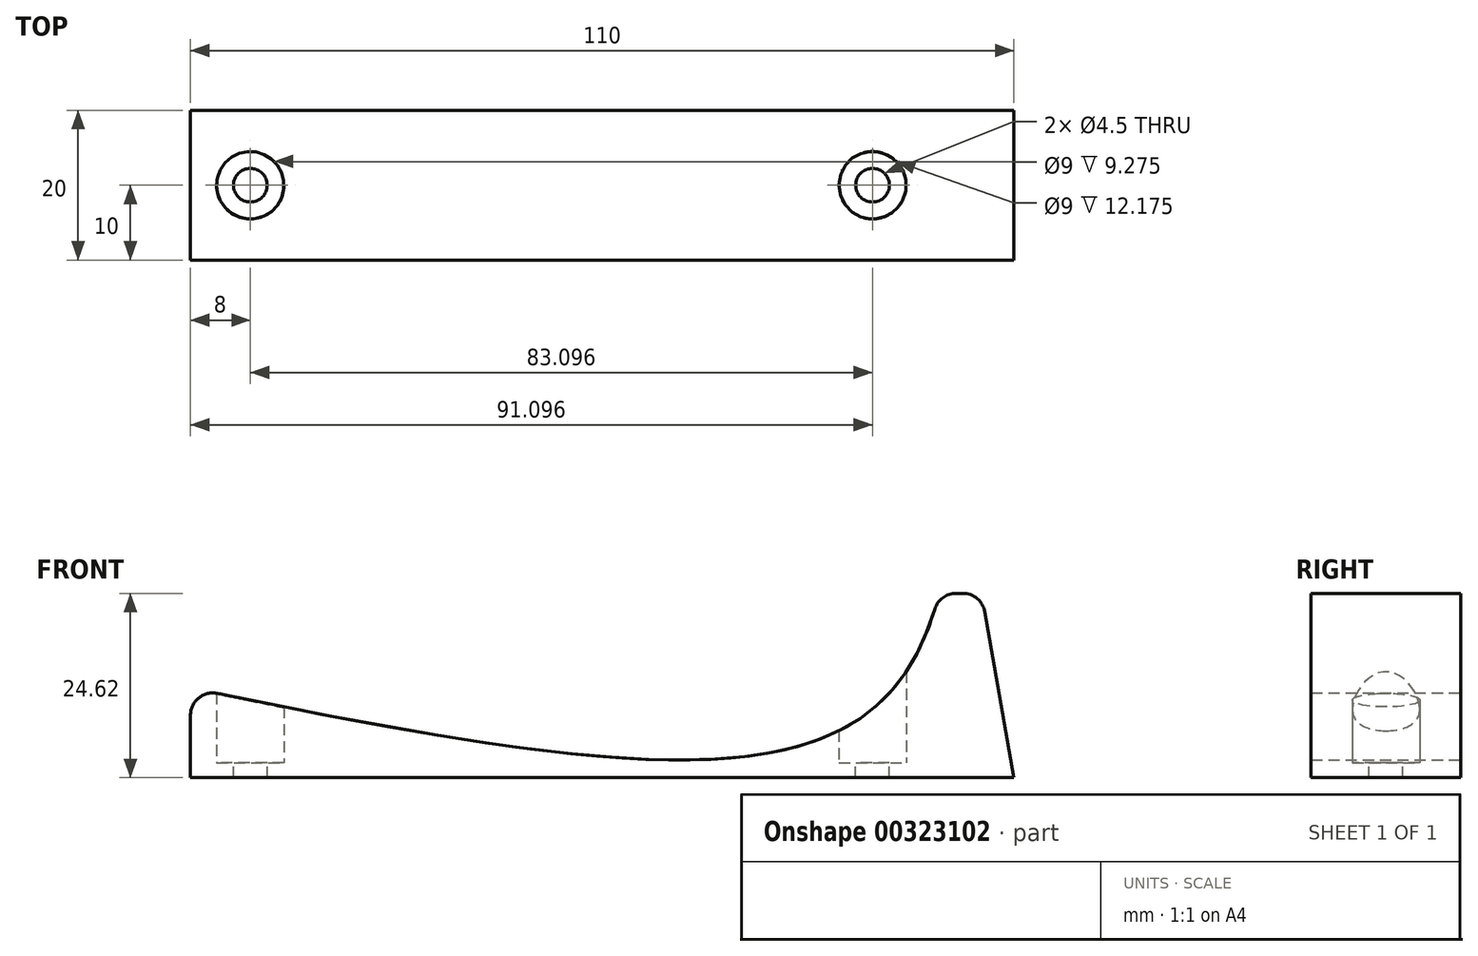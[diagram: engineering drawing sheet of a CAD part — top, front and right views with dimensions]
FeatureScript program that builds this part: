
annotation { "Feature Type Name" : "Feature", "Feature Type Description" : "" }
export const myFeature = defineFeature(function(context is Context, id is Id, definition is map)
    precondition{}
    {
        {
            var Q0;
            Q0=qCreatedBy(makeId("Front.planeOp"),FACE);
            var sketch = newSketch(context, id + "F0", { "sketchPlane" : qUnion([Q0])});
            skFitSpline(sketch, "E0", {"points": [v(0, 12) * mm, v(101.32, 64.38) * mm], "startDerivative": vector(270.11, -56.3) * mm, "endDerivative": vector(-14.41, 200.62) * mm});
            skLineSegment(sketch, "E1", {"start": v(105.66, 24.62) * mm, "end": v(110, 0) * mm});
            skLineSegment(sketch, "E2", {"start": v(110, 0) * mm, "end": v(0, 0) * mm});
            skLineSegment(sketch, "E3", {"start": v(0, 0) * mm, "end": v(0, 12) * mm});
            skLineSegment(sketch, "E4", {"start": v(100, 24.62) * mm, "end": v(105.66, 24.62) * mm});
            skPoint(sketch, "E4.endSnap0", {"position": v(105.66, 32.19) * mm});
            skSolve(sketch);
        }
        {
            var Q0;
            Q0=makeQuery(id+"F0.imprint","IMPRINT",FACE,{"disambiguationData":[TD([[makeQuery(id+"F0.imprint","IMPRINT",EDGE,{"derivedFrom":sQuery(id+"F0.wireOp",EDGE,"E0")}),-1.0]])]});
            extrude(context, id + "F1", {"entities" : qUnion([Q0]), "endBound" : BoundingType.SYMMETRIC, "depth" : 20 * mm});
        }
        {
            var Q0;
            Q0=makeQuery(id+"F1.opExtrude","SWEPT_EDGE",EDGE,{"disambiguationData":[OSD([sQuery(id+"F0.wireOp",EDGE,"E0"),sQuery(id+"F0.wireOp",EDGE,"E3")])]});
            var Q1;
            Q1=makeQuery(id+"F1.opExtrude","SWEPT_EDGE",EDGE,{"disambiguationData":[OSD([sQuery(id+"F0.wireOp",EDGE,"E0"),sQuery(id+"F0.wireOp",EDGE,"E4")])]});
            var Q2;
            Q2=makeQuery(id+"F1.opExtrude","SWEPT_EDGE",EDGE,{"disambiguationData":[OSD([sQuery(id+"F0.wireOp",EDGE,"E1"),sQuery(id+"F0.wireOp",EDGE,"E4")])]});
            fillet(context, id + "F2", {"entities" : qUnion([Q0, Q1, Q2]), "radius" : 3 * mm, "tangentPropagation" : true, "allowEdgeOverflow" : false});
        }
        {
            var Q0;
            Q0=qCreatedBy(makeId("Top.planeOp"),FACE);
            cPlane(context, id + "F3", {"entities" : qUnion([Q0]), "cplaneType" : CPlaneType.OFFSET, "offset" : 2 * mm, "width" : 150 * mm, "height" : 150 * mm});
        }
        {
            var Q0;
            Q0=qCreatedBy(id+"F3.planeOp",FACE);
            var sketch = newSketch(context, id + "F4", { "sketchPlane" : qUnion([Q0])});
            skCircle(sketch, "E5", {"center": v(8, 0) * mm, "radius": 4.5 * mm});
            skCircle(sketch, "E6", {"center": v(91.1, 0) * mm, "radius": 4.5 * mm});
            skSolve(sketch);
        }
        {
            var Q0;
            Q0 = qSketchRegion(id + "F4", true);
            extrude(context, id + "F5", {"entities" : qUnion([Q0]), "operationType" : NewBodyOperationType.REMOVE, "endBound" : BoundingType.THROUGH_ALL, "depth" : 25 * mm});
        }
        {
            var Q0;
            Q0=qCreatedBy(id+"F3.planeOp",FACE);
            var sketch = newSketch(context, id + "F6", { "sketchPlane" : qUnion([Q0])});
            skCircle(sketch, "E7", {"center": v(91.1, 0) * mm, "radius": 2.25 * mm});
            skCircle(sketch, "E8", {"center": v(8, 0) * mm, "radius": 2.25 * mm});
            skCircle(sketch, "E9.1", {"center": v(91.1, 0) * mm, "radius": 4.5 * mm, "construction": true});
            skCircle(sketch, "E10.0", {"center": v(8, 0) * mm, "radius": 4.5 * mm, "construction": true});
            skSolve(sketch);
        }
        {
            var Q0;
            Q0=makeQuery(id+"F6.imprint","IMPRINT",FACE,{"disambiguationData":[TD([[makeQuery(id+"F6.imprint","IMPRINT",EDGE,{"derivedFrom":sQuery(id+"F6.wireOp",EDGE,"E7")}),1.0]])]});
            var Q1;
            Q1=makeQuery(id+"F6.imprint","IMPRINT",FACE,{"disambiguationData":[TD([[makeQuery(id+"F6.imprint","IMPRINT",EDGE,{"derivedFrom":sQuery(id+"F6.wireOp",EDGE,"E8")}),1.0]])]});
            var Q2;
            Q2 = qConstructionFilter(qBodyType(qCreatedBy(id + "F6" ,EDGE), BodyType.WIRE), ConstructionObject.NO);
            extrude(context, id + "F7", {"entities" : qUnion([Q0, Q1]), "operationType" : NewBodyOperationType.REMOVE, "surfaceEntities" : qUnion([Q2]), "endBound" : BoundingType.THROUGH_ALL, "oppositeDirection" : true, "depth" : 25 * mm});
        }
    });
